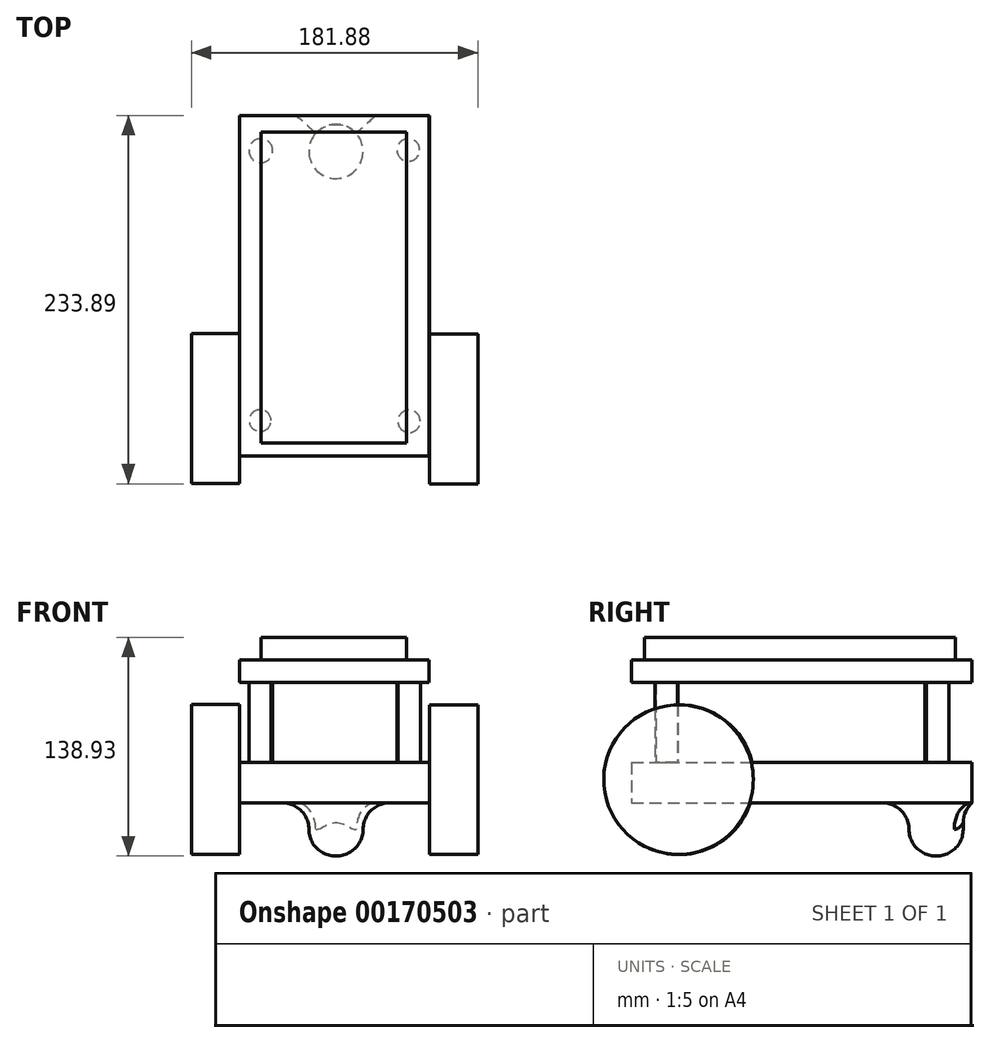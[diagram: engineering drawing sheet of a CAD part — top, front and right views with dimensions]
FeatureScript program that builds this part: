
annotation { "Feature Type Name" : "Feature", "Feature Type Description" : "" }
export const myFeature = defineFeature(function(context is Context, id is Id, definition is map)
    precondition{}
    {
        {
            var Q0;
            Q0=qCreatedBy(makeId("Top.planeOp"),FACE);
            var sketch = newSketch(context, id + "F0", { "sketchPlane" : qUnion([Q0])});
            skLineSegment(sketch, "E0.bottom", {"start": v(59.33, -62.76) * mm, "end": v(-61.08, -62.76) * mm});
            skLineSegment(sketch, "E0.top", {"start": v(59.33, 153.47) * mm, "end": v(-61.08, 153.47) * mm});
            skLineSegment(sketch, "E0.left", {"start": v(59.33, -62.76) * mm, "end": v(59.33, 153.47) * mm});
            skLineSegment(sketch, "E0.right", {"start": v(-61.08, -62.76) * mm, "end": v(-61.08, 153.47) * mm});
            skSolve(sketch);
        }
        {
            var Q0;
            Q0 = qSketchRegion(id + "F0", true);
            extrude(context, id + "F1", {"entities" : qUnion([Q0]), "depth" : 10.92 * mm});
        }
        {
            var Q0;
            Q0=makeQuery(id+"F1.opExtrude","CAP_FACE",FACE,{"disambiguationData":[OSD([sQuery(id+"F0.wireOp",EDGE,"E0.bottom"),sQuery(id+"F0.wireOp",EDGE,"E0.top"),sQuery(id+"F0.wireOp",EDGE,"E0.left"),sQuery(id+"F0.wireOp",EDGE,"E0.right")])],"isStart":true});
            extrude(context, id + "F2", {"entities" : qUnion([Q0]), "operationType" : NewBodyOperationType.ADD, "depth" : 14.73 * mm});
        }
        {
            var Q0;
            {var subQ0=sQuery(id+"F0.wireOp",EDGE,"E0.left");Q0=makeQuery(id+"F2.boolean.opBoolean","MERGE",FACE,{"derivedFrom":[makeQuery(id+"F1.opExtrude","SWEPT_FACE",FACE,{"disambiguationData":[OSD([subQ0])]}),makeQuery(id+"F2.opExtrude","SWEPT_FACE",FACE,{"disambiguationData":[OSD([subQ0])]})]});}
            var sketch = newSketch(context, id + "F3", { "sketchPlane" : qUnion([Q0])});
            skCircle(sketch, "E1", {"center": v(-32.94, 0) * mm, "radius": 47.48 * mm});
            skSolve(sketch);
        }
        {
            var Q0;
            {var subQ1=sQuery(id+"F0.wireOp",EDGE,"E0.left");var subQ6=sQuery(id+"F0.wireOp",EDGE,"E0.bottom");var subQ7=makeQuery(id+"F2.boolean.opBoolean","MERGE",EDGE,{"derivedFrom":[makeQuery(id+"F1.opExtrude","SWEPT_EDGE",EDGE,{"disambiguationData":[OSD([subQ6,subQ1])]}),makeQuery(id+"F2.opExtrude","SWEPT_EDGE",EDGE,{"disambiguationData":[OSD([subQ6,subQ1])]})]});Q0=makeQuery(id+"F3.imprint","IMPRINT",FACE,{"disambiguationData":[TD([[makeQuery(id+"F3.imprint","IMPRINT",EDGE,{"derivedFrom":subQ7}),-1.0]])]});}
            var Q1;
            {var subQ1=sQuery(id+"F0.wireOp",EDGE,"E0.left");var subQ6=sQuery(id+"F0.wireOp",EDGE,"E0.bottom");var subQ7=makeQuery(id+"F2.boolean.opBoolean","MERGE",EDGE,{"derivedFrom":[makeQuery(id+"F1.opExtrude","SWEPT_EDGE",EDGE,{"disambiguationData":[OSD([subQ6,subQ1])]}),makeQuery(id+"F2.opExtrude","SWEPT_EDGE",EDGE,{"disambiguationData":[OSD([subQ6,subQ1])]})]});Q1=makeQuery(id+"F3.imprint","IMPRINT",FACE,{"disambiguationData":[TD([[makeQuery(id+"F3.imprint","IMPRINT",EDGE,{"derivedFrom":subQ7}),1.0]])]});}
            extrude(context, id + "F4", {"entities" : qUnion([Q0, Q1]), "operationType" : NewBodyOperationType.ADD, "depth" : 30.73 * mm});
        }
        {
            var Q0;
            {var subQ0=sQuery(id+"F0.wireOp",EDGE,"E0.right");Q0=makeQuery(id+"F2.boolean.opBoolean","MERGE",FACE,{"derivedFrom":[makeQuery(id+"F1.opExtrude","SWEPT_FACE",FACE,{"disambiguationData":[OSD([subQ0])]}),makeQuery(id+"F2.opExtrude","SWEPT_FACE",FACE,{"disambiguationData":[OSD([subQ0])]})]});}
            var sketch = newSketch(context, id + "F5", { "sketchPlane" : qUnion([Q0])});
            skCircle(sketch, "E2", {"center": v(32.52, 0) * mm, "radius": 47.65 * mm});
            skSolve(sketch);
        }
        {
            var Q0;
            Q0 = qSketchRegion(id + "F5", true);
            extrude(context, id + "F6", {"entities" : qUnion([Q0]), "operationType" : NewBodyOperationType.ADD, "depth" : 30.73 * mm});
        }
        {
            var Q0;
            Q0=makeQuery(id+"F1.opExtrude","CAP_FACE",FACE,{"disambiguationData":[OSD([sQuery(id+"F0.wireOp",EDGE,"E0.bottom"),sQuery(id+"F0.wireOp",EDGE,"E0.top"),sQuery(id+"F0.wireOp",EDGE,"E0.left"),sQuery(id+"F0.wireOp",EDGE,"E0.right")])],"isStart":false});
            var sketch = newSketch(context, id + "F7", { "sketchPlane" : qUnion([Q0])});
            skCircle(sketch, "E3", {"center": v(45.97, 131.57) * mm, "radius": 7.2 * mm});
            skCircle(sketch, "E4", {"center": v(-47.72, 131.12) * mm, "radius": 7.57 * mm});
            skCircle(sketch, "E5", {"center": v(46.43, -40.8) * mm, "radius": 7.12 * mm});
            skCircle(sketch, "E6", {"center": v(-48.17, -40.34) * mm, "radius": 6.94 * mm});
            skSolve(sketch);
        }
        {
            var Q0;
            Q0=makeQuery(id+"F7.imprint","IMPRINT",FACE,{"disambiguationData":[TD([[makeQuery(id+"F7.imprint","IMPRINT",EDGE,{"derivedFrom":sQuery(id+"F7.wireOp",EDGE,"E3")}),1.0]])]});
            var Q1;
            Q1=makeQuery(id+"F7.imprint","IMPRINT",FACE,{"disambiguationData":[TD([[makeQuery(id+"F7.imprint","IMPRINT",EDGE,{"derivedFrom":sQuery(id+"F7.wireOp",EDGE,"E4")}),1.0]])]});
            var Q2;
            Q2=makeQuery(id+"F7.imprint","IMPRINT",FACE,{"disambiguationData":[TD([[makeQuery(id+"F7.imprint","IMPRINT",EDGE,{"derivedFrom":sQuery(id+"F7.wireOp",EDGE,"E5")}),1.0]])]});
            var Q3;
            Q3=makeQuery(id+"F7.imprint","IMPRINT",FACE,{"disambiguationData":[TD([[makeQuery(id+"F7.imprint","IMPRINT",EDGE,{"derivedFrom":sQuery(id+"F7.wireOp",EDGE,"E6")}),1.0]])]});
            extrude(context, id + "F8", {"entities" : qUnion([Q0, Q1, Q2, Q3]), "operationType" : NewBodyOperationType.ADD, "depth" : 50.8 * mm});
        }
        {
            var Q0;
            Q0=makeQuery(id+"F8.opExtrude","CAP_FACE",FACE,{"disambiguationData":[OSD([sQuery(id+"F7.wireOp",EDGE,"E4")])],"isStart":false});
            var sketch = newSketch(context, id + "F9", { "sketchPlane" : qUnion([Q0])});
            skLineSegment(sketch, "E7.bottom", {"start": v(-61.38, 153.33) * mm, "end": v(58.95, 153.33) * mm});
            skLineSegment(sketch, "E7.top", {"start": v(-61.38, -62.68) * mm, "end": v(58.95, -62.68) * mm});
            skLineSegment(sketch, "E7.left", {"start": v(-61.38, 153.33) * mm, "end": v(-61.38, -62.68) * mm});
            skLineSegment(sketch, "E7.right", {"start": v(58.95, 153.33) * mm, "end": v(58.95, -62.68) * mm});
            skSolve(sketch);
        }
        {
            var Q0;
            Q0 = qSketchRegion(id + "F9", true);
            extrude(context, id + "F10", {"entities" : qUnion([Q0]), "operationType" : NewBodyOperationType.ADD, "depth" : 14.22 * mm});
        }
        {
            var Q0;
            Q0=makeQuery(id+"F2.opExtrude","CAP_FACE",FACE,{"disambiguationData":[OSD([sQuery(id+"F0.wireOp",EDGE,"E0.bottom"),sQuery(id+"F0.wireOp",EDGE,"E0.top"),sQuery(id+"F0.wireOp",EDGE,"E0.left"),sQuery(id+"F0.wireOp",EDGE,"E0.right")])],"isStart":false});
            var sketch = newSketch(context, id + "F11", { "sketchPlane" : qUnion([Q0])});
            skCircle(sketch, "E8", {"center": v(0, -130.66) * mm, "radius": 17.21 * mm});
            skSolve(sketch);
        }
        {
            var Q0;
            Q0=makeQuery(id+"F11.imprint","IMPRINT",FACE,{"disambiguationData":[TD([[makeQuery(id+"F11.imprint","IMPRINT",EDGE,{"derivedFrom":sQuery(id+"F11.wireOp",EDGE,"E8")}),1.0]])]});
            extrude(context, id + "F12", {"entities" : qUnion([Q0]), "operationType" : NewBodyOperationType.ADD, "depth" : 33.78 * mm});
        }
        {
            var Q0;
            Q0=makeQuery(id+"F12.opExtrude","SWEPT_FACE",FACE,{"disambiguationData":[OSD([sQuery(id+"F11.wireOp",EDGE,"E8")])]});
            fillet(context, id + "F13", {"entities" : qUnion([Q0]), "radius" : 16.9 * mm, "tangentPropagation" : true, "allowEdgeOverflow" : false});
        }
        {
            var Q0;
            Q0=makeQuery(id+"F10.opExtrude","CAP_FACE",FACE,{"disambiguationData":[OSD([sQuery(id+"F9.wireOp",EDGE,"E7.bottom"),sQuery(id+"F9.wireOp",EDGE,"E7.top"),sQuery(id+"F9.wireOp",EDGE,"E7.left"),sQuery(id+"F9.wireOp",EDGE,"E7.right")])],"isStart":false});
            var sketch = newSketch(context, id + "F14", { "sketchPlane" : qUnion([Q0])});
            skLineSegment(sketch, "E9.bottom", {"start": v(-47.54, 142.98) * mm, "end": v(44.86, 142.98) * mm});
            skLineSegment(sketch, "E9.top", {"start": v(-47.54, -54.58) * mm, "end": v(44.86, -54.58) * mm});
            skLineSegment(sketch, "E9.left", {"start": v(-47.54, 142.98) * mm, "end": v(-47.54, -54.58) * mm});
            skLineSegment(sketch, "E9.right", {"start": v(44.86, 142.98) * mm, "end": v(44.86, -54.58) * mm});
            skSolve(sketch);
        }
        {
            var Q0;
            Q0=makeQuery(id+"F14.imprint","IMPRINT",FACE,{"disambiguationData":[TD([[makeQuery(id+"F14.imprint","IMPRINT",EDGE,{"derivedFrom":sQuery(id+"F14.wireOp",EDGE,"E9.bottom")}),-1.0]])]});
            extrude(context, id + "F15", {"entities" : qUnion([Q0]), "operationType" : NewBodyOperationType.ADD, "depth" : 14.48 * mm});
        }
    });
